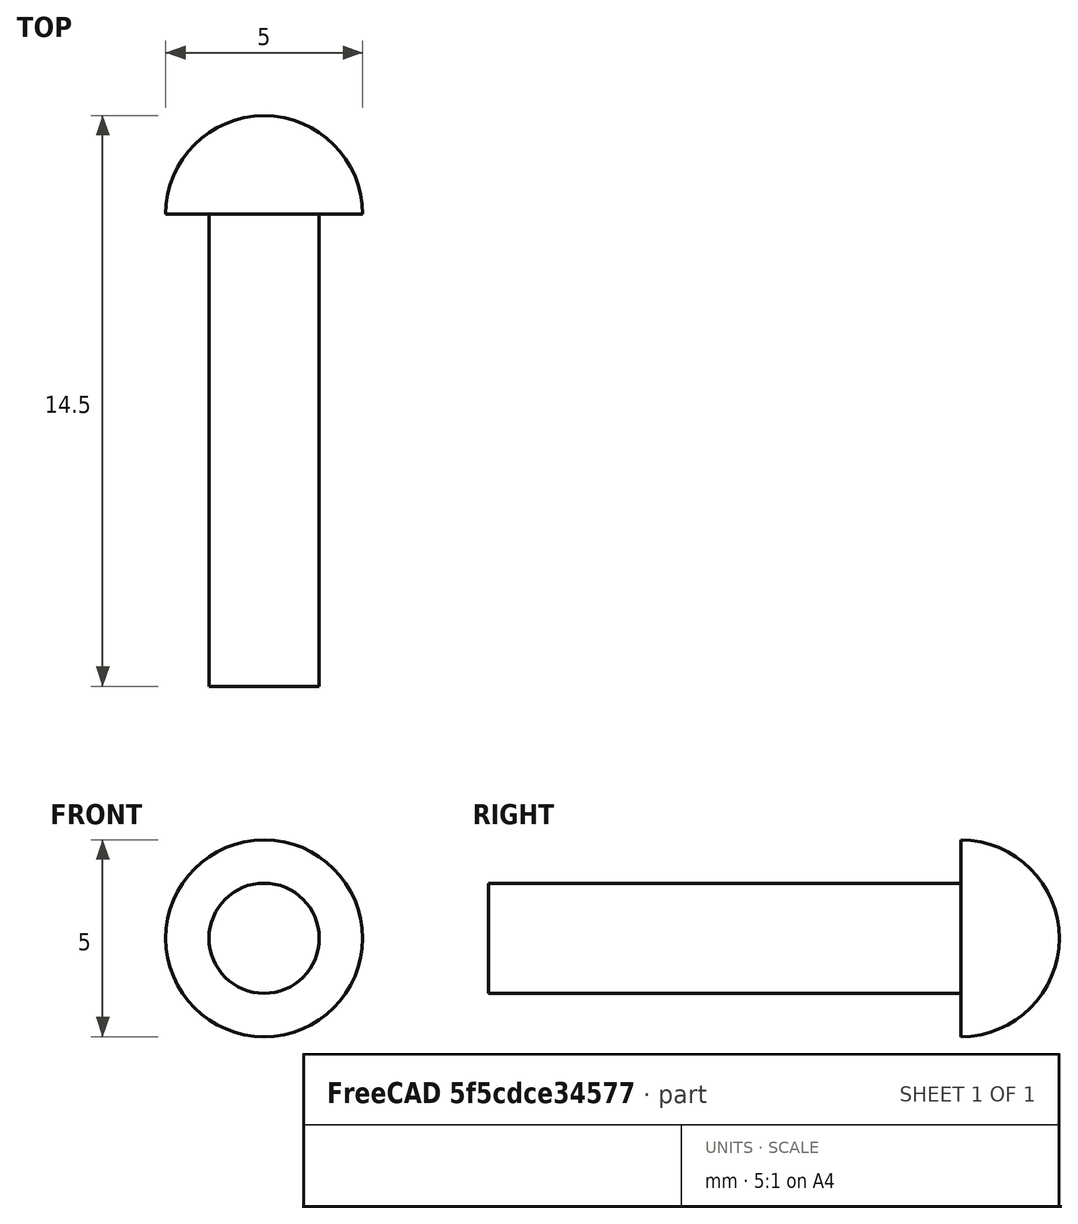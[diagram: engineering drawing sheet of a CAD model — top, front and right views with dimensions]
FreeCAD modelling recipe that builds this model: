
FCSTD DOCUMENT  (FreeCAD 0.19R)
Label: Rivet_12
License: All rights reserved
LicenseURL: http://en.wikipedia.org/wiki/All_rights_reserved
objects: Sketcher::SketchObject×1, PartDesign::Revolution×1, PartDesign::Body×1
note: 4 computed .brp shape members not serialized (recipe doc carries the construction recipe); baked Part::Feature solids carry a one-line shape summary decoded from their .brp

FEATURE [Sketcher::SketchObject] Sketch
  FullyConstrained = true
  MapMode = 5
  Support = -> [XY_Plane]
  sketch-geometry (5):
    g0: LineSegment StartX=0 StartY=0 StartZ=0 EndX=1.4 EndY=0 EndZ=0
    g1: LineSegment StartX=1.4 StartY=0 StartZ=0 EndX=1.4 EndY=12 EndZ=0
    g2: ArcOfCircle CenterX=0 CenterY=12 CenterZ=0 NormalX=0 NormalY=0 NormalZ=1 AngleXU=0 Radius=2.5 StartAngle=2e-16 EndAngle=1.5708
    g3: LineSegment StartX=2e-16 StartY=14.5 StartZ=0 EndX=0 EndY=0 EndZ=0
    g4: LineSegment StartX=1.4 StartY=12 StartZ=0 EndX=2.5 EndY=12 EndZ=0
  constraints (15):
    c: Coincident(g0,g-1)
    c: PointOnObject(g0,g-1)
    c: DistanceX(g0,g0) = 1.4
    c: Coincident(g1,g0)
    c: Vertical(g1)
    c: DistanceY(g1,g1) = 12
    c: PointOnObject(g2,g-2)
    c: PointOnObject(g2,g-2)
    c: Horizontal(g1,g2)
    c: Diameter(g2) = 5
    c: Coincident(g3,g2)
    c: Coincident(g3,g0)
    c: Coincident(g4,g1)
    c: Coincident(g4,g2)
    c: Horizontal(g4)
FEATURE [PartDesign::Revolution] Revolution
  Angle = 360
  Axis = (0,1,0)
  Base = (0,0,0)
  Profile = -> Sketch
  ReferenceAxis = -> Sketch [V_Axis]
  Reversed = true
FEATURE [PartDesign::Body] Body
  Group = -> [Sketch,Revolution]
  Origin = -> Origin
  Tip = -> Revolution
